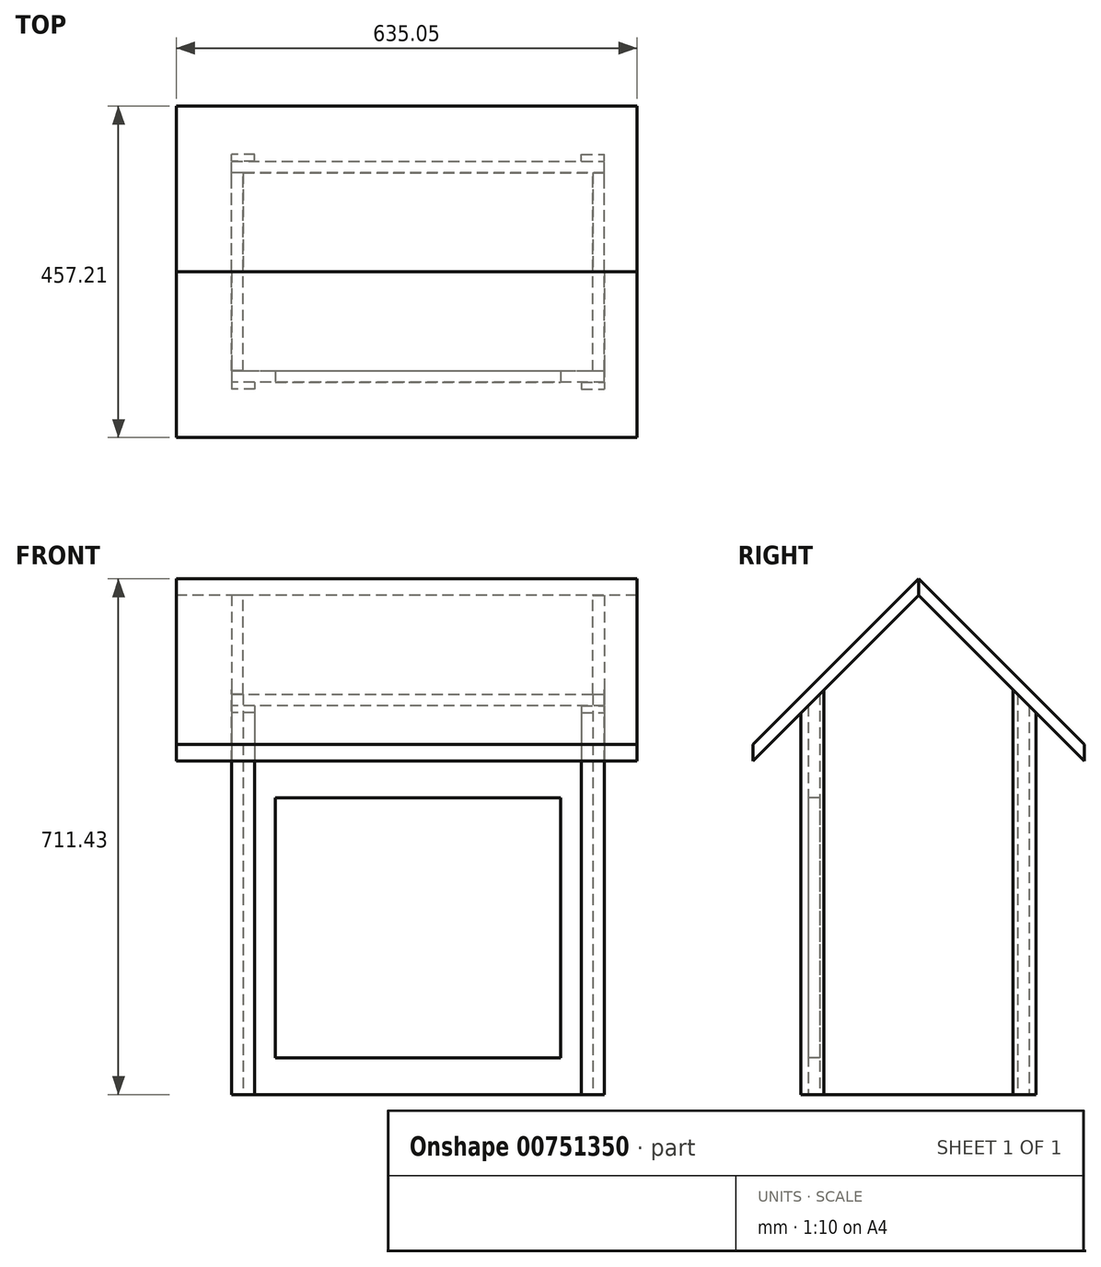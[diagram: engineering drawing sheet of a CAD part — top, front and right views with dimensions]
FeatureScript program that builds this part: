
annotation { "Feature Type Name" : "Feature", "Feature Type Description" : "" }
export const myFeature = defineFeature(function(context is Context, id is Id, definition is map)
    precondition{}
    {
        {
            assignVariable(context, id + "F0", {"name" : "depth", "anyValue" : 273.05 * mm});
        }
        {
            assignVariable(context, id + "F1", {"name" : "width", "anyValue" : 482.6 * mm});
        }
        {
            assignVariable(context, id + "F2", {"name" : "thickness", "anyValue" : 5 / 203.2 * mm});
        }
        {
            assignVariable(context, id + "F3", {"name" : "height", "anyValue" : 688.97 * mm});
        }
        {
            var Q0;
            Q0=qCreatedBy(makeId("Top.planeOp"),FACE);
            var sketch = newSketch(context, id + "F4", { "sketchPlane" : qUnion([Q0])});
            skLineSegment(sketch, "E0.bottom", {"start": v(0, 0) * mm, "end": v(482.6, 0) * mm});
            skLineSegment(sketch, "E0.top", {"start": v(0, 273.05) * mm, "end": v(482.6, 273.05) * mm});
            skLineSegment(sketch, "E0.left", {"start": v(0, 0) * mm, "end": v(0, 273.05) * mm});
            skLineSegment(sketch, "E0.right", {"start": v(482.6, 0) * mm, "end": v(482.6, 273.05) * mm});
            skSolve(sketch);
        }
        {
            var Q0;
            Q0 = qSketchRegion(id + "F4", true);
            extrude(context, id + "F5", {"entities" : qUnion([Q0]), "depth" : getVariable(context, 'thickness'), "offsetDistance" : 25.4 * mm});
        }
        {
            var Q0;
            Q0=makeQuery(id+"F5.opExtrude","CAP_FACE",FACE,{"disambiguationData":[OSD([sQuery(id+"F4.wireOp",EDGE,"E0.bottom"),sQuery(id+"F4.wireOp",EDGE,"E0.top"),sQuery(id+"F4.wireOp",EDGE,"E0.left"),sQuery(id+"F4.wireOp",EDGE,"E0.right")])],"isStart":true});
            var sketch = newSketch(context, id + "F6", { "sketchPlane" : qUnion([Q0])});
            skLineSegment(sketch, "E1.bottom", {"start": v(0, 0) * mm, "end": v(-15.88, 0) * mm});
            skLineSegment(sketch, "E1.top", {"start": v(0, -273.05) * mm, "end": v(-15.87, -273.05) * mm});
            skLineSegment(sketch, "E1.left", {"start": v(0, 0) * mm, "end": v(0, -273.05) * mm});
            skLineSegment(sketch, "E1.right", {"start": v(-15.88, 0) * mm, "end": v(-15.88, -273.05) * mm});
            skSolve(sketch);
        }
        {
            var Q0;
            Q0=makeQuery(id+"F6.imprint","IMPRINT",FACE,{"disambiguationData":[TD([[makeQuery(id+"F6.imprint","IMPRINT",EDGE,{"derivedFrom":sQuery(id+"F6.wireOp",EDGE,"E1.bottom")}),1.0]])]});
            extrude(context, id + "F7", {"entities" : qUnion([Q0]), "oppositeDirection" : true, "depth" : getVariable(context, 'height'), "offsetDistance" : 25.4 * mm});
        }
        {
            var Q0;
            Q0=makeQuery(id+"F7.opExtrude","SWEPT_FACE",FACE,{"disambiguationData":[OSD([sQuery(id+"F6.wireOp",EDGE,"E1.right")])]});
            var sketch = newSketch(context, id + "F8", { "sketchPlane" : qUnion([Q0])});
            skLineSegment(sketch, "E2", {"start": v(-136.53, 688.98) * mm, "end": v(-273.05, 552.45) * mm});
            skLineSegment(sketch, "E3", {"start": v(-273.05, 552.45) * mm, "end": v(-273.05, 688.98) * mm});
            skLineSegment(sketch, "E4", {"start": v(-273.05, 688.98) * mm, "end": v(-136.53, 688.98) * mm});
            skLineSegment(sketch, "E5", {"start": v(-136.53, 688.98) * mm, "end": v(-136.53, 0) * mm, "construction": true});
            skLineSegment(sketch, "E6.MirrorCS", {"start": v(0, 688.98) * mm, "end": v(-136.53, 688.98) * mm});
            skLineSegment(sketch, "E7.MirrorCS", {"start": v(0, 552.45) * mm, "end": v(0, 688.98) * mm});
            skLineSegment(sketch, "E8.MirrorCS", {"start": v(-136.53, 688.98) * mm, "end": v(0, 552.45) * mm});
            skSolve(sketch);
        }
        {
            var Q0;
            Q0 = qSketchRegion(id + "F8", true);
            extrude(context, id + "F9", {"entities" : qUnion([Q0]), "operationType" : NewBodyOperationType.REMOVE, "endBound" : BoundingType.UP_TO_NEXT, "oppositeDirection" : true, "depth" : 25.4 * mm, "offsetDistance" : 25.4 * mm});
        }
        {
            var Q0;
            Q0=qCreatedBy(makeId("Right.planeOp"),FACE);
            cPlane(context, id + "F10", {"entities" : qUnion([Q0]), "cplaneType" : CPlaneType.OFFSET, "offset" : getVariable(context, 'width') / 2, "width" : 152.4 * mm, "height" : 152.4 * mm});
        }
        {
            var Q0;
            Q0=makeQuery(id+"F7.opExtrude","SWEPT_BODY",BODY,{"disambiguationData":[OSD([sQuery(id+"F6.wireOp",EDGE,"E1.bottom"),sQuery(id+"F6.wireOp",EDGE,"E1.top"),sQuery(id+"F6.wireOp",EDGE,"E1.left"),sQuery(id+"F6.wireOp",EDGE,"E1.right")])]});
            var Q1;
            Q1=qCreatedBy(id+"F10.planeOp",FACE);
            mirror(context, id + "F11", {"entities" : qUnion([Q0]), "mirrorPlane" : qUnion([Q1])});
        }
        {
            var Q0;
            Q0=makeQuery(id+"F5.opExtrude","CAP_FACE",FACE,{"disambiguationData":[OSD([sQuery(id+"F4.wireOp",EDGE,"E0.bottom"),sQuery(id+"F4.wireOp",EDGE,"E0.top"),sQuery(id+"F4.wireOp",EDGE,"E0.left"),sQuery(id+"F4.wireOp",EDGE,"E0.right")])],"isStart":true});
            var sketch = newSketch(context, id + "F12", { "sketchPlane" : qUnion([Q0])});
            skLineSegment(sketch, "E9.bottom", {"start": v(498.48, -273.05) * mm, "end": v(-15.87, -273.05) * mm});
            skLineSegment(sketch, "E9.top", {"start": v(498.48, -288.93) * mm, "end": v(-15.87, -288.93) * mm});
            skLineSegment(sketch, "E9.left", {"start": v(498.48, -273.05) * mm, "end": v(498.48, -288.93) * mm});
            skLineSegment(sketch, "E9.right", {"start": v(-15.88, -273.05) * mm, "end": v(-15.87, -288.93) * mm});
            skSolve(sketch);
        }
        {
            var Q0;
            Q0 = qSketchRegion(id + "F12", true);
            extrude(context, id + "F13", {"entities" : qUnion([Q0]), "oppositeDirection" : true, "depth" : (getVariable(context, 'height') - getVariable(context, 'depth') / 2), "offsetDistance" : 25.4 * mm});
        }
        {
            var Q0;
            Q0=makeQuery(id+"F13.opExtrude","SWEPT_FACE",FACE,{"disambiguationData":[OSD([sQuery(id+"F12.wireOp",EDGE,"E9.left")])]});
            var sketch = newSketch(context, id + "F14", { "sketchPlane" : qUnion([Q0])});
            skLineSegment(sketch, "E10", {"start": v(273.05, 552.45) * mm, "end": v(288.93, 536.58) * mm});
            skLineSegment(sketch, "E11", {"start": v(288.93, 536.58) * mm, "end": v(288.93, 552.45) * mm});
            skLineSegment(sketch, "E12", {"start": v(288.93, 552.45) * mm, "end": v(273.05, 552.45) * mm});
            skSolve(sketch);
        }
        {
            var Q0;
            Q0=makeQuery(id+"F14.imprint","IMPRINT",FACE,{"disambiguationData":[TD([[makeQuery(id+"F14.imprint","IMPRINT",EDGE,{"derivedFrom":sQuery(id+"F14.wireOp",EDGE,"E10")}),1.0]])]});
            extrude(context, id + "F15", {"entities" : qUnion([Q0]), "operationType" : NewBodyOperationType.REMOVE, "endBound" : BoundingType.UP_TO_NEXT, "oppositeDirection" : true, "depth" : 25.4 * mm, "offsetDistance" : 25.4 * mm});
        }
        {
            var Q0;
            Q0=makeQuery(id+"F5.opExtrude","CAP_FACE",FACE,{"disambiguationData":[OSD([sQuery(id+"F4.wireOp",EDGE,"E0.bottom"),sQuery(id+"F4.wireOp",EDGE,"E0.top"),sQuery(id+"F4.wireOp",EDGE,"E0.left"),sQuery(id+"F4.wireOp",EDGE,"E0.right")])],"isStart":true});
            var sketch = newSketch(context, id + "F16", { "sketchPlane" : qUnion([Q0])});
            skLineSegment(sketch, "E13.bottom", {"start": v(-15.88, 15.87) * mm, "end": v(498.48, 15.87) * mm});
            skLineSegment(sketch, "E13.top", {"start": v(-15.87, 0) * mm, "end": v(498.48, 0) * mm});
            skLineSegment(sketch, "E13.left", {"start": v(-15.88, 15.87) * mm, "end": v(-15.88, 0) * mm});
            skLineSegment(sketch, "E13.right", {"start": v(498.48, 15.87) * mm, "end": v(498.48, 0) * mm});
            skSolve(sketch);
        }
        {
            var Q0;
            Q0 = qSketchRegion(id + "F16", true);
            extrude(context, id + "F17", {"entities" : qUnion([Q0]), "oppositeDirection" : true, "depth" : getVariable(context, 'height') - getVariable(context, 'depth') / 2, "offsetDistance" : 25.4 * mm});
        }
        {
            var Q0;
            Q0=makeQuery(id+"F17.opExtrude","SWEPT_FACE",FACE,{"disambiguationData":[OSD([sQuery(id+"F16.wireOp",EDGE,"E13.left")])]});
            var sketch = newSketch(context, id + "F18", { "sketchPlane" : qUnion([Q0])});
            skLineSegment(sketch, "E14", {"start": v(0, 552.45) * mm, "end": v(15.87, 536.58) * mm});
            skLineSegment(sketch, "E15", {"start": v(15.87, 536.58) * mm, "end": v(15.87, 552.45) * mm});
            skLineSegment(sketch, "E16", {"start": v(15.87, 552.45) * mm, "end": v(0, 552.45) * mm});
            skSolve(sketch);
        }
        {
            var Q0;
            Q0=makeQuery(id+"F18.imprint","IMPRINT",FACE,{"disambiguationData":[TD([[makeQuery(id+"F18.imprint","IMPRINT",EDGE,{"derivedFrom":sQuery(id+"F18.wireOp",EDGE,"E14")}),1.0]])]});
            extrude(context, id + "F19", {"entities" : qUnion([Q0]), "operationType" : NewBodyOperationType.REMOVE, "endBound" : BoundingType.UP_TO_NEXT, "oppositeDirection" : true, "depth" : 25.4 * mm, "offsetDistance" : 25.4 * mm});
        }
        {
            var Q0;
            Q0=makeQuery(id+"F17.opExtrude","SWEPT_FACE",FACE,{"disambiguationData":[OSD([sQuery(id+"F16.wireOp",EDGE,"E13.bottom")])]});
            var sketch = newSketch(context, id + "F20", { "sketchPlane" : qUnion([Q0])});
            skLineSegment(sketch, "E17.bottom", {"start": v(44.45, 409.58) * mm, "end": v(438.15, 409.58) * mm});
            skLineSegment(sketch, "E17.top", {"start": v(44.45, 50.8) * mm, "end": v(438.15, 50.8) * mm});
            skLineSegment(sketch, "E17.left", {"start": v(44.45, 409.57) * mm, "end": v(44.45, 50.8) * mm});
            skLineSegment(sketch, "E17.right", {"start": v(438.15, 409.58) * mm, "end": v(438.15, 50.8) * mm});
            skLineSegment(sketch, "E18", {"start": v(241.3, 536.58) * mm, "end": v(241.3, 0) * mm, "construction": true});
            skPoint(sketch, "E18.startSnap0", {"position": v(241.3, 0) * mm});
            skPoint(sketch, "E19", {"position": v(241.3, 409.58) * mm});
            skSolve(sketch);
        }
        {
            var Q0;
            Q0 = qSketchRegion(id + "F20", true);
            extrude(context, id + "F21", {"entities" : qUnion([Q0]), "operationType" : NewBodyOperationType.REMOVE, "endBound" : BoundingType.UP_TO_NEXT, "oppositeDirection" : true, "depth" : 25.4 * mm, "offsetDistance" : 25.4 * mm});
        }
        {
            var Q0;
            Q0=makeQuery(id+"F7.opExtrude","SWEPT_FACE",FACE,{"disambiguationData":[OSD([sQuery(id+"F6.wireOp",EDGE,"E1.right")])]});
            var sketch = newSketch(context, id + "F22", { "sketchPlane" : qUnion([Q0])});
            skLineSegment(sketch, "E20", {"start": v(-136.53, 688.98) * mm, "end": v(-136.53, 711.43) * mm});
            skLineSegment(sketch, "E21", {"start": v(-136.53, 711.43) * mm, "end": v(92.08, 482.83) * mm});
            skLineSegment(sketch, "E22", {"start": v(92.07, 482.83) * mm, "end": v(92.07, 460.38) * mm});
            skLineSegment(sketch, "E23", {"start": v(92.07, 460.38) * mm, "end": v(-136.53, 688.98) * mm});
            skSolve(sketch);
        }
        {
            var Q0;
            Q0 = qSketchRegion(id + "F22", true);
            extrude(context, id + "F23", {"entities" : qUnion([Q0]), "oppositeDirection" : true, "depth" : getVariable(context, 'width') + getVariable(context, 'thickness') * 2 + 76.2 * mm, "offsetDistance" : 25.4 * mm, "hasSecondDirection" : true, "secondDirectionOppositeDirection" : false, "secondDirectionDepth" : 76.2 * mm});
        }
        {
            var Q0;
            Q0=qCreatedBy(makeId("Front.planeOp"),FACE);
            cPlane(context, id + "F24", {"entities" : qUnion([Q0]), "cplaneType" : CPlaneType.OFFSET, "offset" : (getVariable(context, 'depth') / 2), "oppositeDirection" : true, "width" : 152.4 * mm, "height" : 152.4 * mm});
        }
        {
            var Q0;
            Q0=makeQuery(id+"F23.opExtrude","SWEPT_BODY",BODY,{"disambiguationData":[OSD([sQuery(id+"F22.wireOp",EDGE,"E20"),sQuery(id+"F22.wireOp",EDGE,"E21"),sQuery(id+"F22.wireOp",EDGE,"E22"),sQuery(id+"F22.wireOp",EDGE,"E23")])]});
            var Q1;
            Q1=qCreatedBy(id+"F24.planeOp",FACE);
            mirror(context, id + "F25", {"entities" : qUnion([Q0]), "mirrorPlane" : qUnion([Q1])});
        }
        {
            assignVariable(context, id + "F26", {"name" : "trim_thickness", "anyValue" : 3 / 203.2 * mm});
        }
        {
            var Q0;
            Q0=makeQuery(id+"F17.opExtrude","SWEPT_FACE",FACE,{"disambiguationData":[OSD([sQuery(id+"F16.wireOp",EDGE,"E13.left")])]});
            var sketch = newSketch(context, id + "F27", { "sketchPlane" : qUnion([Q0])});
            skLineSegment(sketch, "E24", {"start": v(-6.35, 558.8) * mm, "end": v(25.4, 527.05) * mm});
            skLineSegment(sketch, "E25", {"start": v(25.4, 527.05) * mm, "end": v(25.4, 0) * mm});
            skLineSegment(sketch, "E26", {"start": v(25.4, 0) * mm, "end": v(-6.35, 0) * mm});
            skLineSegment(sketch, "E27", {"start": v(-6.35, 0) * mm, "end": v(-6.35, 558.8) * mm});
            skSolve(sketch);
        }
        {
            var Q0;
            Q0 = qSketchRegion(id + "F27", true);
            extrude(context, id + "F28", {"entities" : qUnion([Q0]), "depth" : getVariable(context, 'trim_thickness'), "offsetDistance" : 25.4 * mm});
        }
        {
            var Q0;
            Q0=makeQuery(id+"F28.opExtrude","CAP_FACE",FACE,{"disambiguationData":[OSD([sQuery(id+"F27.wireOp",EDGE,"E24"),sQuery(id+"F27.wireOp",EDGE,"E25"),sQuery(id+"F27.wireOp",EDGE,"E26"),sQuery(id+"F27.wireOp",EDGE,"E27")])],"isStart":true});
            var sketch = newSketch(context, id + "F29", { "sketchPlane" : qUnion([Q0])});
            skLineSegment(sketch, "E28.0", {"start": v(-25.4, 527.05) * mm, "end": v(-25.4, 0) * mm});
            skLineSegment(sketch, "E29.0", {"start": v(-15.87, 536.58) * mm, "end": v(-15.87, 0) * mm});
            skLineSegment(sketch, "E30", {"start": v(-25.4, 527.05) * mm, "end": v(-15.87, 536.58) * mm});
            skLineSegment(sketch, "E31", {"start": v(-25.4, 0) * mm, "end": v(-15.87, 0) * mm});
            skSolve(sketch);
        }
        {
            var Q0;
            Q0 = qSketchRegion(id + "F29", true);
            extrude(context, id + "F30", {"entities" : qUnion([Q0]), "depth" : 31.75 * mm - getVariable(context, 'trim_thickness'), "offsetDistance" : 25.4 * mm});
        }
        {
            var Q0;
            Q0=makeQuery(id+"F30.opExtrude","SWEPT_BODY",BODY,{"disambiguationData":[OSD([sQuery(id+"F29.wireOp",EDGE,"E28.0"),sQuery(id+"F29.wireOp",EDGE,"E29.0"),sQuery(id+"F29.wireOp",EDGE,"E30"),sQuery(id+"F29.wireOp",EDGE,"E31")])]});
            var Q1;
            Q1=makeQuery(id+"F28.opExtrude","SWEPT_BODY",BODY,{"disambiguationData":[OSD([sQuery(id+"F27.wireOp",EDGE,"E24"),sQuery(id+"F27.wireOp",EDGE,"E25"),sQuery(id+"F27.wireOp",EDGE,"E26"),sQuery(id+"F27.wireOp",EDGE,"E27")])]});
            var Q2;
            Q2=qCreatedBy(id+"F24.planeOp",FACE);
            mirror(context, id + "F31", {"entities" : qUnion([Q0, Q1]), "mirrorPlane" : qUnion([Q2])});
        }
        {
            var Q0;
            Q0=makeQuery(id+"F28.opExtrude","SWEPT_BODY",BODY,{"disambiguationData":[OSD([sQuery(id+"F27.wireOp",EDGE,"E24"),sQuery(id+"F27.wireOp",EDGE,"E25"),sQuery(id+"F27.wireOp",EDGE,"E26"),sQuery(id+"F27.wireOp",EDGE,"E27")])]});
            var Q1;
            Q1=makeQuery(id+"F30.opExtrude","SWEPT_BODY",BODY,{"disambiguationData":[OSD([sQuery(id+"F29.wireOp",EDGE,"E28.0"),sQuery(id+"F29.wireOp",EDGE,"E29.0"),sQuery(id+"F29.wireOp",EDGE,"E30"),sQuery(id+"F29.wireOp",EDGE,"E31")])]});
            var Q2;
            Q2=makeQuery(id+"F31.opPattern","COPY",BODY,{"derivedFrom":makeQuery(id+"F28.opExtrude","SWEPT_BODY",BODY,{"disambiguationData":[OSD([sQuery(id+"F27.wireOp",EDGE,"E24"),sQuery(id+"F27.wireOp",EDGE,"E25"),sQuery(id+"F27.wireOp",EDGE,"E26"),sQuery(id+"F27.wireOp",EDGE,"E27")])]}),"instanceName":"1"});
            var Q3;
            Q3=makeQuery(id+"F31.opPattern","COPY",BODY,{"derivedFrom":makeQuery(id+"F30.opExtrude","SWEPT_BODY",BODY,{"disambiguationData":[OSD([sQuery(id+"F29.wireOp",EDGE,"E28.0"),sQuery(id+"F29.wireOp",EDGE,"E29.0"),sQuery(id+"F29.wireOp",EDGE,"E30"),sQuery(id+"F29.wireOp",EDGE,"E31")])]}),"instanceName":"1"});
            var Q4;
            Q4=qCreatedBy(id+"F10.planeOp",FACE);
            mirror(context, id + "F32", {"entities" : qUnion([Q0, Q1, Q2, Q3]), "mirrorPlane" : qUnion([Q4])});
        }
    });
